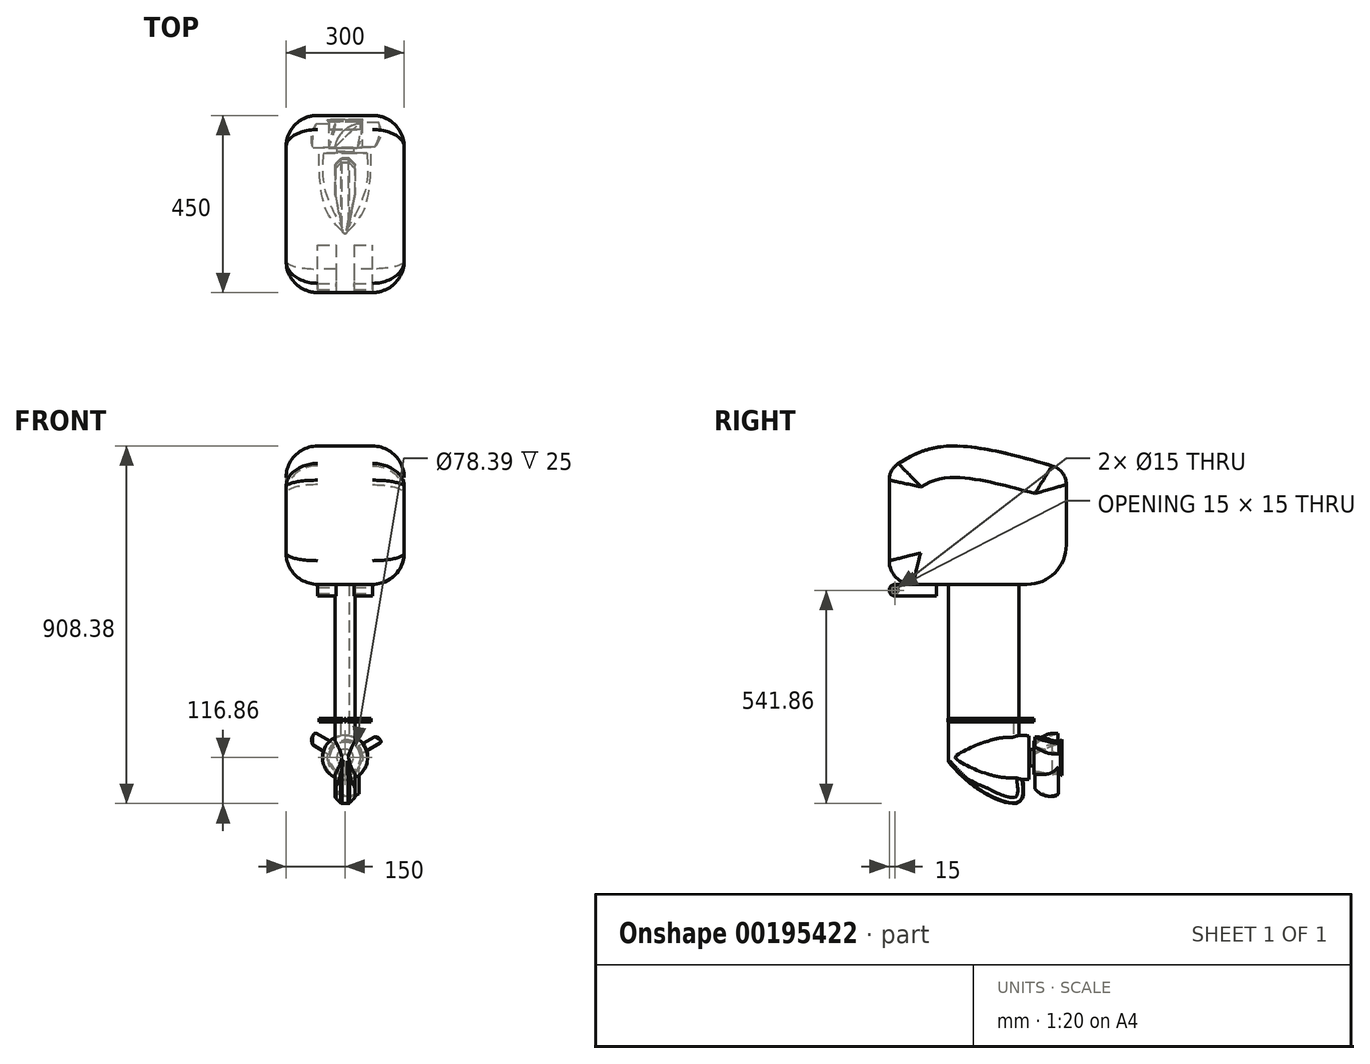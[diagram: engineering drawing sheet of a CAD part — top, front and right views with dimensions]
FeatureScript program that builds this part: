
annotation { "Feature Type Name" : "Feature", "Feature Type Description" : "" }
export const myFeature = defineFeature(function(context is Context, id is Id, definition is map)
    precondition{}
    {
        {
            var Q0;
            Q0=qCreatedBy(makeId("Right.planeOp"),FACE);
            var sketch = newSketch(context, id + "F0", { "sketchPlane" : qUnion([Q0])});
            skLineSegment(sketch, "E0.bottom", {"start": v(0, 0) * mm, "end": v(350, 0) * mm});
            skLineSegment(sketch, "E0.left", {"start": v(0, 0) * mm, "end": v(0, 264.68) * mm});
            skLineSegment(sketch, "E0.right", {"start": v(450, 100) * mm, "end": v(450, 253.23) * mm});
            skFitSpline(sketch, "E1", {"points": [v(0, 291.85) * mm, v(134.26, 350) * mm, v(450, 290.73) * mm], "startDerivative": vector(293.8, 193.4) * mm, "endDerivative": vector(587.22, -172) * mm});
            skPoint(sketch, "E2.visualSharp", {"position": v(450, 0) * mm});
            skArc(sketch, "E3.filletArc", {"start": v(350, 0) * mm, "mid": v(420.71, 29.29) * mm, "end": v(450, 100) * mm});
            skArc(sketch, "E4.filletArc", {"start": v(450, 253.23) * mm, "mid": v(439.98, 283.27) * mm, "end": v(413.92, 301.26) * mm});
            skArc(sketch, "E5.filletArc", {"start": v(23.37, 307) * mm, "mid": v(6.23, 288.86) * mm, "end": v(0, 264.68) * mm});
            skSolve(sketch);
        }
        {
            var Q0;
            Q0=qSketchRegion(id+"F0",true);
            extrude(context, id + "F1", {"entities" : qUnion([Q0]), "endBound" : BoundingType.SYMMETRIC, "depth" : 300 * mm});
        }
        {
            var Q0;
            Q0=makeQuery(id+"F1.opExtrude","SWEPT_EDGE",EDGE,{"disambiguationData":[OSD([sQuery(id+"F0.wireOp",EDGE,"E0.bottom"),sQuery(id+"F0.wireOp",EDGE,"E0.left")])]});
            var Q1;
            Q1=makeQuery(id+"F1.opExtrude","SWEPT_EDGE",EDGE,{"disambiguationData":[OSD([sQuery(id+"F0.wireOp",EDGE,"E0.left"),sQuery(id+"F0.wireOp",EDGE,"E1")])]});
            var Q2;
            Q2=makeQuery(id+"F1.opExtrude","SWEPT_EDGE",EDGE,{"disambiguationData":[OSD([sQuery(id+"F0.wireOp",EDGE,"E0.right"),sQuery(id+"F0.wireOp",EDGE,"E1")])]});
            fillet(context, id + "F2", {"entities" : qUnion([Q0, Q1, Q2]), "radius" : 60 * mm, "tangentPropagation" : true, "allowEdgeOverflow" : false});
        }
        {
            var Q0;
            Q0=makeQuery(id+"F1.opExtrude","CAP_FACE",FACE,{"disambiguationData":[OSD([sQuery(id+"F0.wireOp",EDGE,"E0.bottom"),sQuery(id+"F0.wireOp",EDGE,"E0.left"),sQuery(id+"F0.wireOp",EDGE,"E0.right"),sQuery(id+"F0.wireOp",EDGE,"E1"),sQuery(id+"F0.wireOp",EDGE,"E3.filletArc")])],"isStart":false});
            var Q1;
            Q1=makeQuery(id+"F1.opExtrude","CAP_FACE",FACE,{"disambiguationData":[OSD([sQuery(id+"F0.wireOp",EDGE,"E0.bottom"),sQuery(id+"F0.wireOp",EDGE,"E0.left"),sQuery(id+"F0.wireOp",EDGE,"E0.right"),sQuery(id+"F0.wireOp",EDGE,"E1"),sQuery(id+"F0.wireOp",EDGE,"E3.filletArc")])],"isStart":true});
            fillet(context, id + "F3", {"entities" : qUnion([Q0, Q1]), "radius" : 80 * mm, "tangentPropagation" : true, "allowEdgeOverflow" : false});
        }
        {
            var Q0;
            Q0=qCreatedBy(makeId("Right.planeOp"),FACE);
            var sketch = newSketch(context, id + "F4", { "sketchPlane" : qUnion([Q0])});
            skLineSegment(sketch, "E6.bottom", {"start": v(150, 0) * mm, "end": v(330, 0) * mm});
            skLineSegment(sketch, "E6.left", {"start": v(150, 0) * mm, "end": v(150, -450) * mm});
            skLineSegment(sketch, "E6.right", {"start": v(330, 0) * mm, "end": v(330, -450) * mm});
            skFitSpline(sketch, "E7", {"points": [v(150, -450) * mm, v(230.96, -523.6) * mm, v(331.12, -552.8) * mm, v(330, -450) * mm], "startDerivative": vector(197.7, -227.42) * mm, "endDerivative": vector(-88.88, 410.14) * mm});
            skSolve(sketch);
        }
        {
            var Q0;
            Q0=makeQuery(id+"F4.imprint","IMPRINT",FACE,{"disambiguationData":[TD([[makeQuery(id+"F4.imprint","IMPRINT",EDGE,{"derivedFrom":sQuery(id+"F4.wireOp",EDGE,"E6.bottom")}),-1.0]])]});
            extrude(context, id + "F5", {"entities" : qUnion([Q0]), "operationType" : NewBodyOperationType.ADD, "endBound" : BoundingType.SYMMETRIC, "depth" : 50 * mm});
        }
        {
            var Q0;
            Q0=makeQuery(id+"F5.opExtrude","CAP_EDGE",EDGE,{"disambiguationData":[OSD([sQuery(id+"F4.wireOp",EDGE,"E6.left")])],"isStart":false});
            var Q1;
            Q1=makeQuery(id+"F5.opExtrude","CAP_EDGE",EDGE,{"disambiguationData":[OSD([sQuery(id+"F4.wireOp",EDGE,"E6.left")])],"isStart":true});
            chamfer(context, id + "F6", {"entities" : qUnion([Q0, Q1]), "chamferType" : ChamferType.TWO_OFFSETS, "width1" : 100 * mm, "oppositeDirection" : false, "width2" : 20 * mm, "tangentPropagation" : true});
        }
        {
            var Q0;
            Q0=makeQuery(id+"F5.opExtrude","CAP_EDGE",EDGE,{"disambiguationData":[OSD([sQuery(id+"F4.wireOp",EDGE,"E6.right")])],"isStart":false});
            var Q1;
            Q1=makeQuery(id+"F5.opExtrude","CAP_EDGE",EDGE,{"disambiguationData":[OSD([sQuery(id+"F4.wireOp",EDGE,"E6.right")])],"isStart":true});
            var Q2;
            Q2=makeQuery(id+"F5.opExtrude","CAP_EDGE",EDGE,{"disambiguationData":[OSD([sQuery(id+"F4.wireOp",EDGE,"E7")])],"isStart":true});
            var Q3;
            Q3=makeQuery(id+"F5.opExtrude","CAP_EDGE",EDGE,{"disambiguationData":[OSD([sQuery(id+"F4.wireOp",EDGE,"E7")])],"isStart":false});
            chamfer(context, id + "F7", {"entities" : qUnion([Q0, Q1, Q2, Q3]), "width" : 15 * mm, "tangentPropagation" : true});
        }
        {
            var Q0;
            Q0=qCreatedBy(makeId("Top.planeOp"),FACE);
            cPlane(context, id + "F8", {"entities" : qUnion([Q0]), "cplaneType" : CPlaneType.OFFSET, "offset" : 440 * mm, "oppositeDirection" : true, "width" : 150 * mm, "height" : 150 * mm});
        }
        {
            var Q0;
            Q0=qCreatedBy(makeId("Top.planeOp"),FACE);
            cPlane(context, id + "F9", {"entities" : qUnion([Q0]), "cplaneType" : CPlaneType.OFFSET, "offset" : 350 * mm, "oppositeDirection" : true, "width" : 150 * mm, "height" : 150 * mm});
        }
        {
            var Q0;
            Q0=qCreatedBy(id+"F9.planeOp",FACE);
            var sketch = newSketch(context, id + "F10", { "sketchPlane" : qUnion([Q0])});
            skLineSegment(sketch, "E8", {"start": v(0, 0) * mm, "end": v(0, 609.27) * mm, "construction": true});
            skFitSpline(sketch, "E9", {"points": [v(0, 149.18) * mm, v(48.96, 211.78) * mm, v(66.59, 367.97) * mm], "startDerivative": vector(136.03, 126.4) * mm, "endDerivative": vector(4.54, 301.34) * mm});
            skLineSegment(sketch, "E10", {"start": v(66.59, 367.97) * mm, "end": v(0, 367.97) * mm});
            skLineSegment(sketch, "E11.MirrorCS", {"start": v(-66.59, 367.97) * mm, "end": v(0, 367.97) * mm});
            skFitSpline(sketch, "E12.MirrorCS", {"points": [v(0, 149.18) * mm, v(-48.96, 211.78) * mm, v(-66.59, 367.97) * mm], "startDerivative": vector(-136.03, 126.4) * mm, "endDerivative": vector(-4.54, 301.34) * mm});
            skSolve(sketch);
        }
        {
            var Q0;
            Q0=makeQuery(id+"F10.imprint","IMPRINT",FACE,{"disambiguationData":[TD([[makeQuery(id+"F10.imprint","IMPRINT",EDGE,{"derivedFrom":sQuery(id+"F10.wireOp",EDGE,"E9")}),1.0]])]});
            extrude(context, id + "F11", {"entities" : qUnion([Q0]), "operationType" : NewBodyOperationType.ADD, "depth" : 10 * mm});
        }
        {
            var Q0;
            Q0=qCreatedBy(id+"F8.planeOp",FACE);
            var sketch = newSketch(context, id + "F12", { "sketchPlane" : qUnion([Q0])});
            skLineSegment(sketch, "E13", {"start": v(0, 0) * mm, "end": v(0, 598.5) * mm, "construction": true});
            skFitSpline(sketch, "E14", {"points": [v(0, 153.19) * mm, v(52.22, 263.58) * mm, v(55.2, 354.59) * mm], "startDerivative": vector(121.68, 208.22) * mm, "endDerivative": vector(-14.61, 194.24) * mm});
            skLineSegment(sketch, "E15", {"start": v(55.2, 354.59) * mm, "end": v(0, 354.59) * mm});
            skLineSegment(sketch, "E16", {"start": v(0, 354.59) * mm, "end": v(0, 153.19) * mm});
            skLineSegment(sketch, "E17", {"start": v(0, 153.19) * mm, "end": v(0, 354.59) * mm});
            skSolve(sketch);
        }
        {
            var Q0;
            Q0=makeQuery(id+"F12.imprint","IMPRINT",FACE,{"disambiguationData":[TD([[makeQuery(id+"F12.imprint","IMPRINT",EDGE,{"derivedFrom":sQuery(id+"F12.wireOp",EDGE,"E14")}),1.0]])]});
            var Q1;
            Q1=sQuery(id+"F12.wireOp",EDGE,"E13");
            revolve(context, id + "F13", {"operationType" : NewBodyOperationType.ADD, "entities" : qUnion([Q0]), "axis" : qUnion([Q1]), "revolveType" : RevolveType.FULL});
        }
        {
            var Q0;
            Q0=qCreatedBy(id+"F8.planeOp",FACE);
            var sketch = newSketch(context, id + "F14", { "sketchPlane" : qUnion([Q0])});
            skLineSegment(sketch, "E18", {"start": v(0, 0) * mm, "end": v(0, 577.62) * mm, "construction": true});
            skLineSegment(sketch, "E19", {"start": v(42.52, 367.27) * mm, "end": v(42.52, 434.4) * mm});
            skLineSegment(sketch, "E20", {"start": v(42.52, 434.4) * mm, "end": v(45.6, 438.87) * mm});
            skLineSegment(sketch, "E21", {"start": v(45.6, 438.87) * mm, "end": v(0, 438.87) * mm});
            skLineSegment(sketch, "E22", {"start": v(0, 438.87) * mm, "end": v(0, 367.27) * mm});
            skLineSegment(sketch, "E23", {"start": v(21.26, 367.27) * mm, "end": v(42.52, 367.27) * mm});
            skLineSegment(sketch, "E24", {"start": v(0, 476.76) * mm, "end": v(0, 352.88) * mm, "construction": true});
            skLineSegment(sketch, "E25", {"start": v(21.26, 367.27) * mm, "end": v(21.26, 357.45) * mm});
            skPoint(sketch, "E25.endSnap0", {"position": v(21.26, 367.27) * mm});
            skLineSegment(sketch, "E26", {"start": v(21.26, 357.45) * mm, "end": v(0, 352.88) * mm});
            skLineSegment(sketch, "E27", {"start": v(0, 367.27) * mm, "end": v(0, 352.88) * mm});
            skSolve(sketch);
        }
        {
            var Q0;
            Q0=makeQuery(id+"F14.imprint","IMPRINT",FACE,{"disambiguationData":[TD([[makeQuery(id+"F14.imprint","IMPRINT",EDGE,{"derivedFrom":sQuery(id+"F14.wireOp",EDGE,"E19")}),1.0]])]});
            var Q1;
            Q1=sQuery(id+"F14.wireOp",EDGE,"E18");
            revolve(context, id + "F15", {"operationType" : NewBodyOperationType.ADD, "entities" : qUnion([Q0]), "axis" : qUnion([Q1]), "revolveType" : RevolveType.FULL});
        }
        {
            var Q0;
            Q0=qCreatedBy(id+"F8.planeOp",FACE);
            var sketch = newSketch(context, id + "F16", { "sketchPlane" : qUnion([Q0])});
            skLineSegment(sketch, "E28", {"start": v(-25.58, 369.64) * mm, "end": v(35.48, 429.61) * mm});
            skArc(sketch, "E29", {"start": v(35.48, 429.61) * mm, "mid": v(-4.9, 409.65) * mm, "end": v(-25.58, 369.64) * mm});
            skSolve(sketch);
        }
        {
            var Q0;
            Q0=qSketchRegion(id+"F16",true);
            extrude(context, id + "F17", {"entities" : qUnion([Q0]), "operationType" : NewBodyOperationType.ADD, "oppositeDirection" : true, "depth" : 100 * mm});
        }
        {
            var Q0;
            Q0=makeQuery(id+"F17.opExtrude","SWEPT_FACE",FACE,{"disambiguationData":[OSD([sQuery(id+"F16.wireOp",EDGE,"E28")])]});
            var sketch = newSketch(context, id + "F18", { "sketchPlane" : qUnion([Q0])});
            skArc(sketch, "E30", {"start": v(240.76, -519.29) * mm, "mid": v(281.8, -537.46) * mm, "end": v(326.34, -532) * mm});
            skLineSegment(sketch, "E31", {"start": v(326.34, -532) * mm, "end": v(326.34, -552.5) * mm});
            skLineSegment(sketch, "E32", {"start": v(326.34, -552.5) * mm, "end": v(240.76, -552.5) * mm});
            skLineSegment(sketch, "E33", {"start": v(240.76, -552.5) * mm, "end": v(240.76, -519.29) * mm});
            skSolve(sketch);
        }
        {
            var Q0;
            {var subQ0=sQuery(id+"F18.wireOp",EDGE,"E30");Q0=makeQuery(id+"F18.imprint","IMPRINT",FACE,{"disambiguationData":[TD([[makeQuery(id+"F18.imprint","IMPRINT",EDGE,{"derivedFrom":subQ0}),-1.0]])]});}
            extrude(context, id + "F19", {"entities" : qUnion([Q0]), "operationType" : NewBodyOperationType.REMOVE, "oppositeDirection" : true, "depth" : 25 * mm});
        }
        {
            var Q0;
            Q0=qCreatedBy(id+"F8.planeOp",FACE);
            var sketch = newSketch(context, id + "F20", { "sketchPlane" : qUnion([Q0])});
            skLineSegment(sketch, "E34", {"start": v(0, 0) * mm, "end": v(0, -579.96) * mm, "construction": true});
            skSolve(sketch);
        }
        {
            var Q0;
            Q0=qCreatedBy(id+"F8.planeOp",FACE);
            var Q1;
            Q1=sQuery(id+"F20.wireOp",EDGE,"E34");
            cPlane(context, id + "F21", {"entities" : qUnion([Q0, Q1]), "cplaneType" : CPlaneType.LINE_ANGLE, "offset" : 25 * mm, "angle" : 120 * degree, "width" : 150 * mm, "height" : 150 * mm});
        }
        {
            var Q0;
            Q0=qCreatedBy(id+"F21.planeOp",FACE);
            var sketch = newSketch(context, id + "F22", { "sketchPlane" : qUnion([Q0])});
            skLineSegment(sketch, "E35", {"start": v(369.75, -372.98) * mm, "end": v(431.09, -393.02) * mm});
            skArc(sketch, "E36", {"start": v(369.75, -372.98) * mm, "mid": v(398.1, -390.1) * mm, "end": v(431.09, -393.02) * mm});
            skSolve(sketch);
        }
        {
            var Q0;
            Q0=qSketchRegion(id+"F22",true);
            extrude(context, id + "F23", {"entities" : qUnion([Q0]), "operationType" : NewBodyOperationType.ADD, "depth" : 100 * mm});
        }
        {
            var Q0;
            Q0=qCreatedBy(id+"F8.planeOp",FACE);
            var Q1;
            Q1=sQuery(id+"F20.wireOp",EDGE,"E34");
            cPlane(context, id + "F24", {"entities" : qUnion([Q0, Q1]), "cplaneType" : CPlaneType.LINE_ANGLE, "offset" : 25 * mm, "angle" : 240 * degree, "width" : 150 * mm, "height" : 150 * mm});
        }
        {
            var Q0;
            Q0=qCreatedBy(id+"F24.planeOp",FACE);
            var sketch = newSketch(context, id + "F25", { "sketchPlane" : qUnion([Q0])});
            skLineSegment(sketch, "E37", {"start": v(-428.8, -364.5) * mm, "end": v(-368.38, -394.59) * mm});
            skArc(sketch, "E38", {"start": v(-368.38, -394.59) * mm, "mid": v(-395.28, -372.9) * mm, "end": v(-428.8, -364.5) * mm});
            skSolve(sketch);
        }
        {
            var Q0;
            Q0=qSketchRegion(id+"F25",true);
            extrude(context, id + "F26", {"entities" : qUnion([Q0]), "operationType" : NewBodyOperationType.ADD, "depth" : 100 * mm});
        }
        {
            var Q0;
            Q0=makeQuery(id+"F26.opExtrude","SWEPT_FACE",FACE,{"disambiguationData":[OSD([sQuery(id+"F25.wireOp",EDGE,"E37")])]});
            var sketch = newSketch(context, id + "F27", { "sketchPlane" : qUnion([Q0])});
            skArc(sketch, "E39", {"start": v(167.44, -115.72) * mm, "mid": v(164.28, -150.5) * mm, "end": v(177.43, -182.85) * mm});
            skLineSegment(sketch, "E40", {"start": v(177.43, -182.85) * mm, "end": v(132.7, -194.37) * mm});
            skLineSegment(sketch, "E41", {"start": v(132.7, -194.37) * mm, "end": v(114.24, -122.69) * mm});
            skLineSegment(sketch, "E42", {"start": v(114.24, -122.69) * mm, "end": v(167.44, -115.72) * mm});
            skSolve(sketch);
        }
        {
            var Q0;
            {var subQ0=sQuery(id+"F27.wireOp",EDGE,"E39");Q0=makeQuery(id+"F27.imprint","IMPRINT",FACE,{"disambiguationData":[TD([[makeQuery(id+"F27.imprint","IMPRINT",EDGE,{"derivedFrom":subQ0}),-1.0]])]});}
            extrude(context, id + "F28", {"entities" : qUnion([Q0]), "operationType" : NewBodyOperationType.REMOVE, "oppositeDirection" : true, "depth" : 25 * mm});
        }
        {
            var Q0;
            Q0=makeQuery(id+"F23.opExtrude","SWEPT_FACE",FACE,{"disambiguationData":[OSD([sQuery(id+"F22.wireOp",EDGE,"E35")])]});
            var sketch = newSketch(context, id + "F29", { "sketchPlane" : qUnion([Q0])});
            skArc(sketch, "E43", {"start": v(-44.35, 482.72) * mm, "mid": v(-30.38, 512.89) * mm, "end": v(-32.1, 546.08) * mm});
            skLineSegment(sketch, "E44", {"start": v(-32.1, 546.08) * mm, "end": v(-7.37, 541.64) * mm});
            skLineSegment(sketch, "E45", {"start": v(-7.37, 541.64) * mm, "end": v(-19.2, 475.68) * mm});
            skLineSegment(sketch, "E46", {"start": v(-19.2, 475.68) * mm, "end": v(-44.35, 482.72) * mm});
            skSolve(sketch);
        }
        {
            var Q0;
            {var subQ0=sQuery(id+"F29.wireOp",EDGE,"E43");Q0=makeQuery(id+"F29.imprint","IMPRINT",FACE,{"disambiguationData":[TD([[makeQuery(id+"F29.imprint","IMPRINT",EDGE,{"derivedFrom":subQ0}),-1.0]])]});}
            extrude(context, id + "F30", {"entities" : qUnion([Q0]), "operationType" : NewBodyOperationType.REMOVE, "oppositeDirection" : true, "depth" : 25 * mm});
        }
        {
            var Q0;
            Q0=makeQuery(id+"F15.opRevolve","SWEPT_FACE",FACE,{"disambiguationData":[OSD([sQuery(id+"F14.wireOp",EDGE,"E21")])]});
            var sketch = newSketch(context, id + "F31", { "sketchPlane" : qUnion([Q0])});
            skCircle(sketch, "E47", {"center": v(0, -440) * mm, "radius": 39.2 * mm});
            skSolve(sketch);
        }
        {
            var Q0;
            Q0=makeQuery(id+"F31.imprint","IMPRINT",FACE,{"disambiguationData":[TD([[makeQuery(id+"F31.imprint","IMPRINT",EDGE,{"derivedFrom":sQuery(id+"F31.wireOp",EDGE,"E47")}),1.0]])]});
            extrude(context, id + "F32", {"entities" : qUnion([Q0]), "operationType" : NewBodyOperationType.REMOVE, "oppositeDirection" : true, "depth" : 25 * mm});
        }
        {
            var Q0;
            Q0=makeQuery(id+"F1.opExtrude","SWEPT_FACE",FACE,{"disambiguationData":[OSD([sQuery(id+"F0.wireOp",EDGE,"E0.bottom")])]});
            var sketch = newSketch(context, id + "F33", { "sketchPlane" : qUnion([Q0])});
            skLineSegment(sketch, "E48.bottom", {"start": v(-70, 0) * mm, "end": v(-23.33, 0) * mm});
            skLineSegment(sketch, "E48.top", {"start": v(-70, -120) * mm, "end": v(-23.33, -120) * mm});
            skLineSegment(sketch, "E48.left", {"start": v(-70, 0) * mm, "end": v(-70, -120) * mm});
            skLineSegment(sketch, "E48.right", {"start": v(70, 0) * mm, "end": v(70, -120) * mm});
            skPoint(sketch, "E48.middle", {"position": v(0, -60) * mm});
            skLineSegment(sketch, "E49.top", {"start": v(-23.33, 0) * mm, "end": v(23.33, 0) * mm});
            skLineSegment(sketch, "E49.left", {"start": v(-23.33, -120) * mm, "end": v(-23.33, 0) * mm});
            skLineSegment(sketch, "E49.right", {"start": v(23.33, -120) * mm, "end": v(23.33, 0) * mm});
            skLineSegment(sketch, "E50.trimOffspring", {"start": v(23.33, 0) * mm, "end": v(70, 0) * mm});
            skLineSegment(sketch, "E51.trimOffspring", {"start": v(23.33, -120) * mm, "end": v(70, -120) * mm});
            skSolve(sketch);
        }
        {
            var Q0;
            Q0=qSketchRegion(id+"F33",true);
            extrude(context, id + "F34", {"entities" : qUnion([Q0]), "operationType" : NewBodyOperationType.ADD, "depth" : 30 * mm});
        }
        {
            var Q0;
            {var subQ0=sQuery(id+"F4.wireOp",EDGE,"E6.left");Q0=makeQuery(id+"F6.opChamfer","BLEND_EDGE",EDGE,{"blendedFrom":[makeQuery(id+"F5.opExtrude","CAP_EDGE",EDGE,{"disambiguationData":[OSD([subQ0])],"isStart":false}),makeQuery(id+"F5.opExtrude","SWEPT_FACE",FACE,{"disambiguationData":[OSD([subQ0])]})],"blendedInto":[makeQuery(id+"F5.opExtrude","SWEPT_FACE",FACE,{"disambiguationData":[OSD([subQ0])]})]});}
            var Q1;
            {var subQ0=sQuery(id+"F4.wireOp",EDGE,"E6.left");Q1=makeQuery(id+"F6.opChamfer","BLEND_EDGE",EDGE,{"blendedFrom":[makeQuery(id+"F5.opExtrude","CAP_EDGE",EDGE,{"disambiguationData":[OSD([subQ0])],"isStart":true}),makeQuery(id+"F5.opExtrude","SWEPT_FACE",FACE,{"disambiguationData":[OSD([subQ0])]})],"blendedInto":[makeQuery(id+"F5.opExtrude","SWEPT_FACE",FACE,{"disambiguationData":[OSD([subQ0])]})]});}
            var Q2;
            Q2=makeQuery(id+"F5.opExtrude","SWEPT_EDGE",EDGE,{"disambiguationData":[OSD([sQuery(id+"F4.wireOp",EDGE,"E6.left"),sQuery(id+"F4.wireOp",EDGE,"E7")])]});
            var Q3;
            {var subQ0=sQuery(id+"F4.wireOp",EDGE,"E7");Q3=makeQuery(id+"F7.opChamfer","BLEND_EDGE",EDGE,{"blendedFrom":[makeQuery(id+"F5.opExtrude","CAP_EDGE",EDGE,{"disambiguationData":[OSD([subQ0])],"isStart":false}),makeQuery(id+"F5.opExtrude","SWEPT_FACE",FACE,{"disambiguationData":[OSD([subQ0])]})],"blendedInto":[makeQuery(id+"F5.opExtrude","SWEPT_FACE",FACE,{"disambiguationData":[OSD([subQ0])]})]});}
            var Q4;
            {var subQ0=sQuery(id+"F4.wireOp",EDGE,"E7");Q4=makeQuery(id+"F7.opChamfer","BLEND_EDGE",EDGE,{"blendedFrom":[makeQuery(id+"F5.opExtrude","CAP_EDGE",EDGE,{"disambiguationData":[OSD([subQ0])],"isStart":true}),makeQuery(id+"F5.opExtrude","SWEPT_FACE",FACE,{"disambiguationData":[OSD([subQ0])]})],"blendedInto":[makeQuery(id+"F5.opExtrude","SWEPT_FACE",FACE,{"disambiguationData":[OSD([subQ0])]})]});}
            var Q5;
            Q5=makeQuery(id+"F6.opChamfer","BLEND_EDGE",EDGE,{"blendedFrom":[makeQuery(id+"F5.opExtrude","CAP_EDGE",EDGE,{"disambiguationData":[OSD([sQuery(id+"F4.wireOp",EDGE,"E6.left")])],"isStart":false}),makeQuery(id+"F5.opExtrude","SWEPT_FACE",FACE,{"disambiguationData":[OSD([sQuery(id+"F4.wireOp",EDGE,"E7")])]})],"blendedInto":[makeQuery(id+"F5.opExtrude","SWEPT_FACE",FACE,{"disambiguationData":[OSD([sQuery(id+"F4.wireOp",EDGE,"E7")])]})]});
            var Q6;
            {var subQ0=sQuery(id+"F4.wireOp",EDGE,"E6.left");var subQ1=makeQuery(id+"F5.opExtrude","CAP_FACE",FACE,{"disambiguationData":[OSD([sQuery(id+"F4.wireOp",EDGE,"E6.bottom"),subQ0,sQuery(id+"F4.wireOp",EDGE,"E6.right"),sQuery(id+"F4.wireOp",EDGE,"E7")])],"isStart":false});var subQ2=makeQuery(id+"F5.opExtrude","CAP_EDGE",EDGE,{"disambiguationData":[OSD([subQ0])],"isStart":false});Q6=makeQuery(id+"F11.boolean.opBoolean","SPLIT",EDGE,{"disambiguationData":[TD([makeQuery(id+"F1.opExtrude","SWEPT_FACE",FACE,{"disambiguationData":[OSD([sQuery(id+"F0.wireOp",EDGE,"E0.bottom")])]})])],"derivedFrom":makeQuery(id+"F6.opChamfer","BLEND_EDGE",EDGE,{"blendedFrom":[subQ2,subQ1],"blendedInto":[subQ1]})});}
            var Q7;
            {var subQ0=sQuery(id+"F4.wireOp",EDGE,"E7");var subQ1=sQuery(id+"F4.wireOp",EDGE,"E6.left");var subQ2=makeQuery(id+"F5.opExtrude","CAP_FACE",FACE,{"disambiguationData":[OSD([sQuery(id+"F4.wireOp",EDGE,"E6.bottom"),subQ1,sQuery(id+"F4.wireOp",EDGE,"E6.right"),subQ0])],"isStart":false});var subQ3=makeQuery(id+"F11.opExtrude","CAP_FACE",FACE,{"disambiguationData":[OSD([sQuery(id+"F10.wireOp",EDGE,"E9"),sQuery(id+"F10.wireOp",EDGE,"E10"),sQuery(id+"F10.wireOp",EDGE,"E11.MirrorCS"),sQuery(id+"F10.wireOp",EDGE,"E12.MirrorCS")])],"isStart":true});var subQ4=makeQuery(id+"F5.opExtrude","CAP_EDGE",EDGE,{"disambiguationData":[OSD([subQ1])],"isStart":false});Q7=makeQuery(id+"F13.boolean.opBoolean","SPLIT",EDGE,{"disambiguationData":[TD([subQ3])],"derivedFrom":makeQuery(id+"F11.boolean.opBoolean","SPLIT",EDGE,{"disambiguationData":[TD([makeQuery(id+"F7.opChamfer","BLEND_FACE",FACE,{"disambiguationData":[OSD([subQ0]),TDD([makeQuery(id+"F5.opExtrude","CAP_EDGE",EDGE,{"disambiguationData":[OSD([subQ0])],"isStart":false})])]})])],"derivedFrom":makeQuery(id+"F6.opChamfer","BLEND_EDGE",EDGE,{"blendedFrom":[subQ4,subQ2],"blendedInto":[subQ2]})})});}
            var Q8;
            {var subQ0=sQuery(id+"F4.wireOp",EDGE,"E7");var subQ1=sQuery(id+"F4.wireOp",EDGE,"E6.left");var subQ2=makeQuery(id+"F5.opExtrude","CAP_FACE",FACE,{"disambiguationData":[OSD([sQuery(id+"F4.wireOp",EDGE,"E6.bottom"),subQ1,sQuery(id+"F4.wireOp",EDGE,"E6.right"),subQ0])],"isStart":false});var subQ3=makeQuery(id+"F5.opExtrude","CAP_EDGE",EDGE,{"disambiguationData":[OSD([subQ1])],"isStart":false});var subQ5=makeQuery(id+"F7.opChamfer","BLEND_FACE",FACE,{"disambiguationData":[OSD([subQ0]),TDD([makeQuery(id+"F5.opExtrude","CAP_EDGE",EDGE,{"disambiguationData":[OSD([subQ0])],"isStart":false})])]});Q8=makeQuery(id+"F13.boolean.opBoolean","SPLIT",EDGE,{"disambiguationData":[TD([subQ5])],"derivedFrom":makeQuery(id+"F11.boolean.opBoolean","SPLIT",EDGE,{"disambiguationData":[TD([subQ5])],"derivedFrom":makeQuery(id+"F6.opChamfer","BLEND_EDGE",EDGE,{"blendedFrom":[subQ3,subQ2],"blendedInto":[subQ2]})})});}
            var Q9;
            {var subQ0=sQuery(id+"F4.wireOp",EDGE,"E6.left");var subQ1=makeQuery(id+"F5.opExtrude","CAP_FACE",FACE,{"disambiguationData":[OSD([sQuery(id+"F4.wireOp",EDGE,"E6.bottom"),subQ0,sQuery(id+"F4.wireOp",EDGE,"E6.right"),sQuery(id+"F4.wireOp",EDGE,"E7")])],"isStart":true});var subQ2=makeQuery(id+"F5.opExtrude","CAP_EDGE",EDGE,{"disambiguationData":[OSD([subQ0])],"isStart":true});Q9=makeQuery(id+"F11.boolean.opBoolean","SPLIT",EDGE,{"disambiguationData":[TD([makeQuery(id+"F1.opExtrude","SWEPT_FACE",FACE,{"disambiguationData":[OSD([sQuery(id+"F0.wireOp",EDGE,"E0.bottom")])]})])],"derivedFrom":makeQuery(id+"F6.opChamfer","BLEND_EDGE",EDGE,{"blendedFrom":[subQ2,subQ1],"blendedInto":[subQ1]})});}
            var Q10;
            {var subQ0=sQuery(id+"F4.wireOp",EDGE,"E7");var subQ1=sQuery(id+"F4.wireOp",EDGE,"E6.left");var subQ2=makeQuery(id+"F5.opExtrude","CAP_FACE",FACE,{"disambiguationData":[OSD([sQuery(id+"F4.wireOp",EDGE,"E6.bottom"),subQ1,sQuery(id+"F4.wireOp",EDGE,"E6.right"),subQ0])],"isStart":true});var subQ3=makeQuery(id+"F5.opExtrude","CAP_EDGE",EDGE,{"disambiguationData":[OSD([subQ1])],"isStart":true});var subQ5=makeQuery(id+"F11.opExtrude","CAP_FACE",FACE,{"disambiguationData":[OSD([sQuery(id+"F10.wireOp",EDGE,"E9"),sQuery(id+"F10.wireOp",EDGE,"E10"),sQuery(id+"F10.wireOp",EDGE,"E11.MirrorCS"),sQuery(id+"F10.wireOp",EDGE,"E12.MirrorCS")])],"isStart":true});Q10=makeQuery(id+"F13.boolean.opBoolean","SPLIT",EDGE,{"disambiguationData":[TD([subQ5])],"derivedFrom":makeQuery(id+"F11.boolean.opBoolean","SPLIT",EDGE,{"disambiguationData":[TD([makeQuery(id+"F7.opChamfer","BLEND_FACE",FACE,{"disambiguationData":[OSD([subQ0]),TDD([makeQuery(id+"F5.opExtrude","CAP_EDGE",EDGE,{"disambiguationData":[OSD([subQ0])],"isStart":true})])]})])],"derivedFrom":makeQuery(id+"F6.opChamfer","BLEND_EDGE",EDGE,{"blendedFrom":[subQ3,subQ2],"blendedInto":[subQ2]})})});}
            var Q11;
            {var subQ0=sQuery(id+"F4.wireOp",EDGE,"E6.right");var subQ1=makeQuery(id+"F5.opExtrude","CAP_FACE",FACE,{"disambiguationData":[OSD([sQuery(id+"F4.wireOp",EDGE,"E6.bottom"),sQuery(id+"F4.wireOp",EDGE,"E6.left"),subQ0,sQuery(id+"F4.wireOp",EDGE,"E7")])],"isStart":true});var subQ2=makeQuery(id+"F5.opExtrude","CAP_EDGE",EDGE,{"disambiguationData":[OSD([subQ0])],"isStart":true});Q11=makeQuery(id+"F11.boolean.opBoolean","SPLIT",EDGE,{"disambiguationData":[TD([makeQuery(id+"F1.opExtrude","SWEPT_FACE",FACE,{"disambiguationData":[OSD([sQuery(id+"F0.wireOp",EDGE,"E0.bottom")])]})])],"derivedFrom":makeQuery(id+"F7.opChamfer","BLEND_EDGE",EDGE,{"blendedFrom":[subQ2,subQ1],"blendedInto":[subQ1]})});}
            var Q12;
            {var subQ0=sQuery(id+"F4.wireOp",EDGE,"E6.right");var subQ1=makeQuery(id+"F5.opExtrude","SWEPT_FACE",FACE,{"disambiguationData":[OSD([subQ0])]});var subQ2=makeQuery(id+"F5.opExtrude","CAP_EDGE",EDGE,{"disambiguationData":[OSD([subQ0])],"isStart":true});Q12=makeQuery(id+"F11.boolean.opBoolean","SPLIT",EDGE,{"disambiguationData":[TD([makeQuery(id+"F1.opExtrude","SWEPT_FACE",FACE,{"disambiguationData":[OSD([sQuery(id+"F0.wireOp",EDGE,"E0.bottom")])]})])],"derivedFrom":makeQuery(id+"F7.opChamfer","BLEND_EDGE",EDGE,{"blendedFrom":[subQ2,subQ1],"blendedInto":[subQ1]})});}
            var Q13;
            {var subQ0=sQuery(id+"F4.wireOp",EDGE,"E6.right");var subQ1=makeQuery(id+"F5.opExtrude","CAP_FACE",FACE,{"disambiguationData":[OSD([sQuery(id+"F4.wireOp",EDGE,"E6.bottom"),sQuery(id+"F4.wireOp",EDGE,"E6.left"),subQ0,sQuery(id+"F4.wireOp",EDGE,"E7")])],"isStart":false});var subQ2=makeQuery(id+"F5.opExtrude","CAP_EDGE",EDGE,{"disambiguationData":[OSD([subQ0])],"isStart":false});Q13=makeQuery(id+"F11.boolean.opBoolean","SPLIT",EDGE,{"disambiguationData":[TD([makeQuery(id+"F1.opExtrude","SWEPT_FACE",FACE,{"disambiguationData":[OSD([sQuery(id+"F0.wireOp",EDGE,"E0.bottom")])]})])],"derivedFrom":makeQuery(id+"F7.opChamfer","BLEND_EDGE",EDGE,{"blendedFrom":[subQ2,subQ1],"blendedInto":[subQ1]})});}
            var Q14;
            {var subQ0=sQuery(id+"F4.wireOp",EDGE,"E7");var subQ1=sQuery(id+"F4.wireOp",EDGE,"E6.right");var subQ2=makeQuery(id+"F5.opExtrude","CAP_FACE",FACE,{"disambiguationData":[OSD([sQuery(id+"F4.wireOp",EDGE,"E6.bottom"),sQuery(id+"F4.wireOp",EDGE,"E6.left"),subQ1,subQ0])],"isStart":false});var subQ3=makeQuery(id+"F5.opExtrude","CAP_EDGE",EDGE,{"disambiguationData":[OSD([subQ1])],"isStart":false});Q14=makeQuery(id+"F11.boolean.opBoolean","SPLIT",EDGE,{"disambiguationData":[TD([makeQuery(id+"F7.opChamfer","BLEND_FACE",FACE,{"disambiguationData":[OSD([subQ0]),TDD([makeQuery(id+"F5.opExtrude","CAP_EDGE",EDGE,{"disambiguationData":[OSD([subQ0])],"isStart":false})])]})])],"derivedFrom":makeQuery(id+"F7.opChamfer","BLEND_EDGE",EDGE,{"blendedFrom":[subQ3,subQ2],"blendedInto":[subQ2]})});}
            var Q15;
            {var subQ0=sQuery(id+"F4.wireOp",EDGE,"E7");var subQ1=sQuery(id+"F4.wireOp",EDGE,"E6.left");var subQ2=makeQuery(id+"F5.opExtrude","CAP_FACE",FACE,{"disambiguationData":[OSD([sQuery(id+"F4.wireOp",EDGE,"E6.bottom"),subQ1,sQuery(id+"F4.wireOp",EDGE,"E6.right"),subQ0])],"isStart":true});var subQ3=makeQuery(id+"F5.opExtrude","CAP_EDGE",EDGE,{"disambiguationData":[OSD([subQ1])],"isStart":true});var subQ5=makeQuery(id+"F7.opChamfer","BLEND_FACE",FACE,{"disambiguationData":[OSD([subQ0]),TDD([makeQuery(id+"F5.opExtrude","CAP_EDGE",EDGE,{"disambiguationData":[OSD([subQ0])],"isStart":true})])]});Q15=makeQuery(id+"F13.boolean.opBoolean","SPLIT",EDGE,{"disambiguationData":[TD([subQ5])],"derivedFrom":makeQuery(id+"F11.boolean.opBoolean","SPLIT",EDGE,{"disambiguationData":[TD([subQ5])],"derivedFrom":makeQuery(id+"F6.opChamfer","BLEND_EDGE",EDGE,{"blendedFrom":[subQ3,subQ2],"blendedInto":[subQ2]})})});}
            var Q16;
            {var subQ0=sQuery(id+"F4.wireOp",EDGE,"E7");Q16=makeQuery(id+"F7.opChamfer","BLEND_EDGE",EDGE,{"blendedFrom":[makeQuery(id+"F5.opExtrude","CAP_EDGE",EDGE,{"disambiguationData":[OSD([subQ0])],"isStart":true}),makeQuery(id+"F5.opExtrude","CAP_FACE",FACE,{"disambiguationData":[OSD([sQuery(id+"F4.wireOp",EDGE,"E6.bottom"),sQuery(id+"F4.wireOp",EDGE,"E6.left"),sQuery(id+"F4.wireOp",EDGE,"E6.right"),subQ0])],"isStart":true})],"blendedInto":[makeQuery(id+"F5.opExtrude","CAP_FACE",FACE,{"disambiguationData":[OSD([sQuery(id+"F4.wireOp",EDGE,"E6.bottom"),sQuery(id+"F4.wireOp",EDGE,"E6.left"),sQuery(id+"F4.wireOp",EDGE,"E6.right"),subQ0])],"isStart":true})]});}
            fillet(context, id + "F35", {"entities" : qUnion([Q0, Q1, Q2, Q3, Q4, Q5, Q6, Q7, Q8, Q9, Q10, Q11, Q12, Q13, Q14, Q15, Q16]), "radius" : 5 * mm, "tangentPropagation" : true, "allowEdgeOverflow" : false});
        }
        {
            var Q0;
            Q0=makeQuery(id+"F34.opExtrude","CAP_EDGE",EDGE,{"disambiguationData":[OSD([sQuery(id+"F33.wireOp",EDGE,"E48.bottom")])],"isStart":false});
            var Q1;
            Q1=makeQuery(id+"F34.opExtrude","CAP_EDGE",EDGE,{"disambiguationData":[OSD([sQuery(id+"F33.wireOp",EDGE,"E48.bottom")])],"isStart":true});
            var Q2;
            Q2=makeQuery(id+"F34.opExtrude","CAP_EDGE",EDGE,{"disambiguationData":[OSD([sQuery(id+"F33.wireOp",EDGE,"E50.trimOffspring")])],"isStart":false});
            var Q3;
            Q3=makeQuery(id+"F34.opExtrude","CAP_EDGE",EDGE,{"disambiguationData":[OSD([sQuery(id+"F33.wireOp",EDGE,"E50.trimOffspring")])],"isStart":true});
            fillet(context, id + "F36", {"entities" : qUnion([Q0, Q1, Q2, Q3]), "radius" : 15 * mm, "tangentPropagation" : true, "allowEdgeOverflow" : false});
        }
        {
            var Q0;
            Q0=makeQuery(id+"F34.opExtrude","SWEPT_FACE",FACE,{"disambiguationData":[OSD([sQuery(id+"F33.wireOp",EDGE,"E48.right")])]});
            var sketch = newSketch(context, id + "F37", { "sketchPlane" : qUnion([Q0])});
            skCircle(sketch, "E52", {"center": v(15, -15) * mm, "radius": 7.5 * mm});
            skSolve(sketch);
        }
        {
            var Q0;
            Q0=makeQuery(id+"F37.imprint","IMPRINT",FACE,{"disambiguationData":[TD([[makeQuery(id+"F37.imprint","IMPRINT",EDGE,{"derivedFrom":sQuery(id+"F37.wireOp",EDGE,"E52")}),1.0]])]});
            var Q1;
            Q1=makeQuery(id+"F34.opExtrude","SWEPT_FACE",FACE,{"disambiguationData":[OSD([sQuery(id+"F33.wireOp",EDGE,"E48.left")])]});
            extrude(context, id + "F38", {"entities" : qUnion([Q0]), "operationType" : NewBodyOperationType.REMOVE, "endBound" : BoundingType.UP_TO_SURFACE, "oppositeDirection" : true, "endBoundEntityFace" : qUnion([Q1]), "depth" : 120 * mm});
        }
    });
